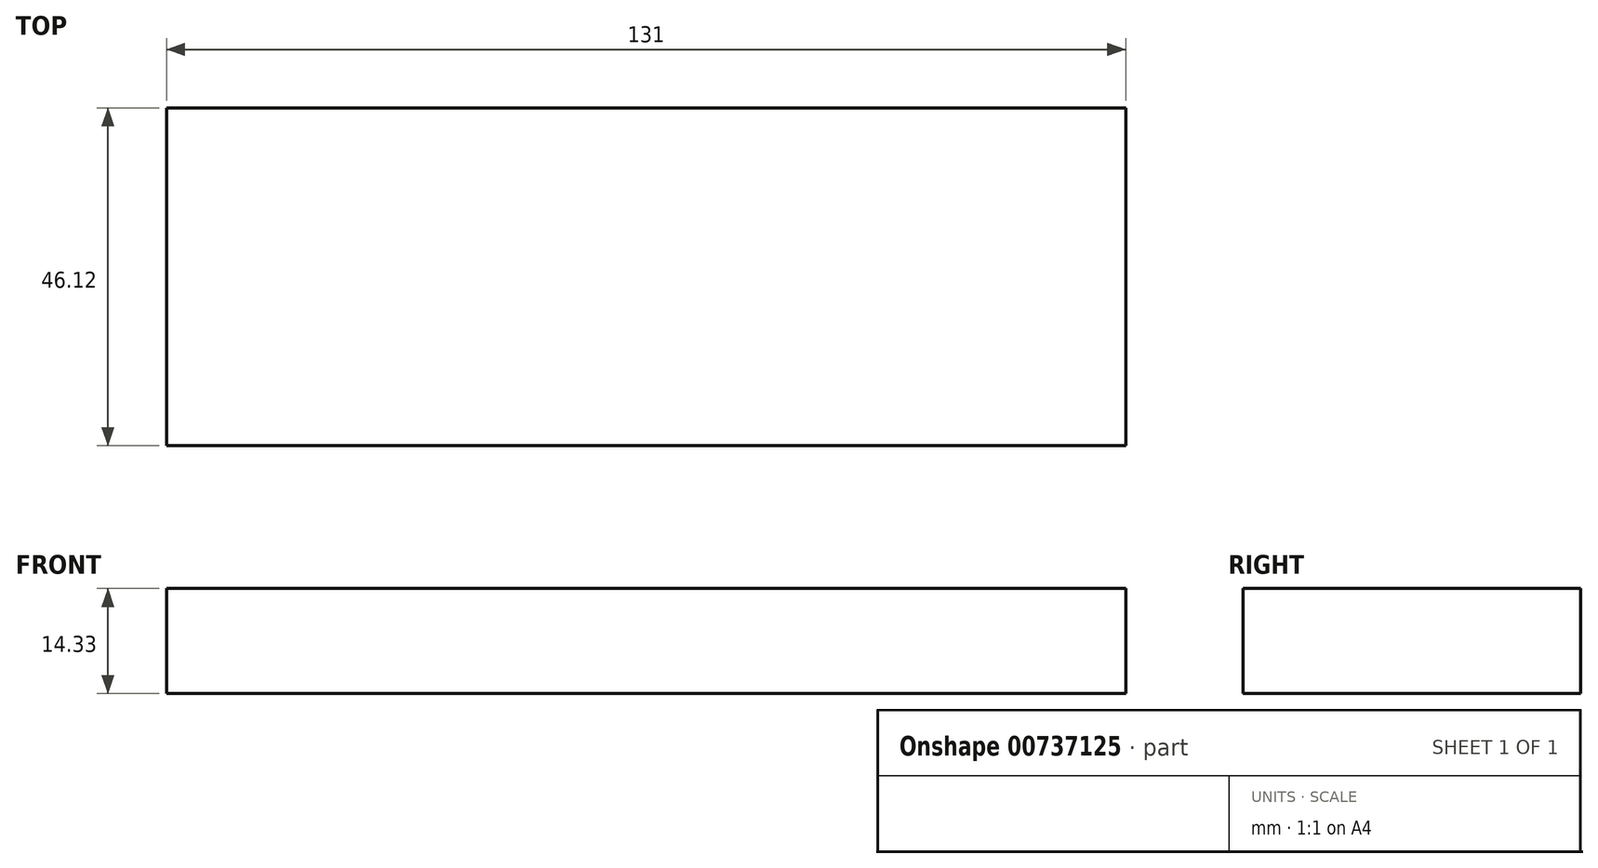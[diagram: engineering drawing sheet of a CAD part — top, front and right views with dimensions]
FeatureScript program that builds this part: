
annotation { "Feature Type Name" : "Feature", "Feature Type Description" : "" }
export const myFeature = defineFeature(function(context is Context, id is Id, definition is map)
    precondition{}
    {
        {
            var Q0;
            Q0=qCreatedBy(makeId("Top.planeOp"),FACE);
            var sketch = newSketch(context, id + "F0", { "sketchPlane" : qUnion([Q0])});
            skLineSegment(sketch, "E0.bottom", {"start": v(65.5, -23.06) * mm, "end": v(-65.5, -23.06) * mm});
            skLineSegment(sketch, "E0.top", {"start": v(65.5, 23.06) * mm, "end": v(-65.5, 23.06) * mm});
            skLineSegment(sketch, "E0.left", {"start": v(65.5, -23.06) * mm, "end": v(65.5, 23.06) * mm});
            skLineSegment(sketch, "E0.right", {"start": v(-65.5, -23.06) * mm, "end": v(-65.5, 23.06) * mm});
            skPoint(sketch, "E0.middle", {"position": v(0, 0) * mm});
            skSolve(sketch);
        }
        {
            var Q0;
            Q0=makeQuery(id+"F0.imprint","IMPRINT",FACE,{"disambiguationData":[TD([[makeQuery(id+"F0.imprint","IMPRINT",EDGE,{"derivedFrom":sQuery(id+"F0.wireOp",EDGE,"E0.bottom")}),-1.0]])]});
            extrude(context, id + "F1", {"entities" : qUnion([Q0]), "depth" : 14.33 * mm, "offsetDistance" : 25.4 * mm});
        }
    });
